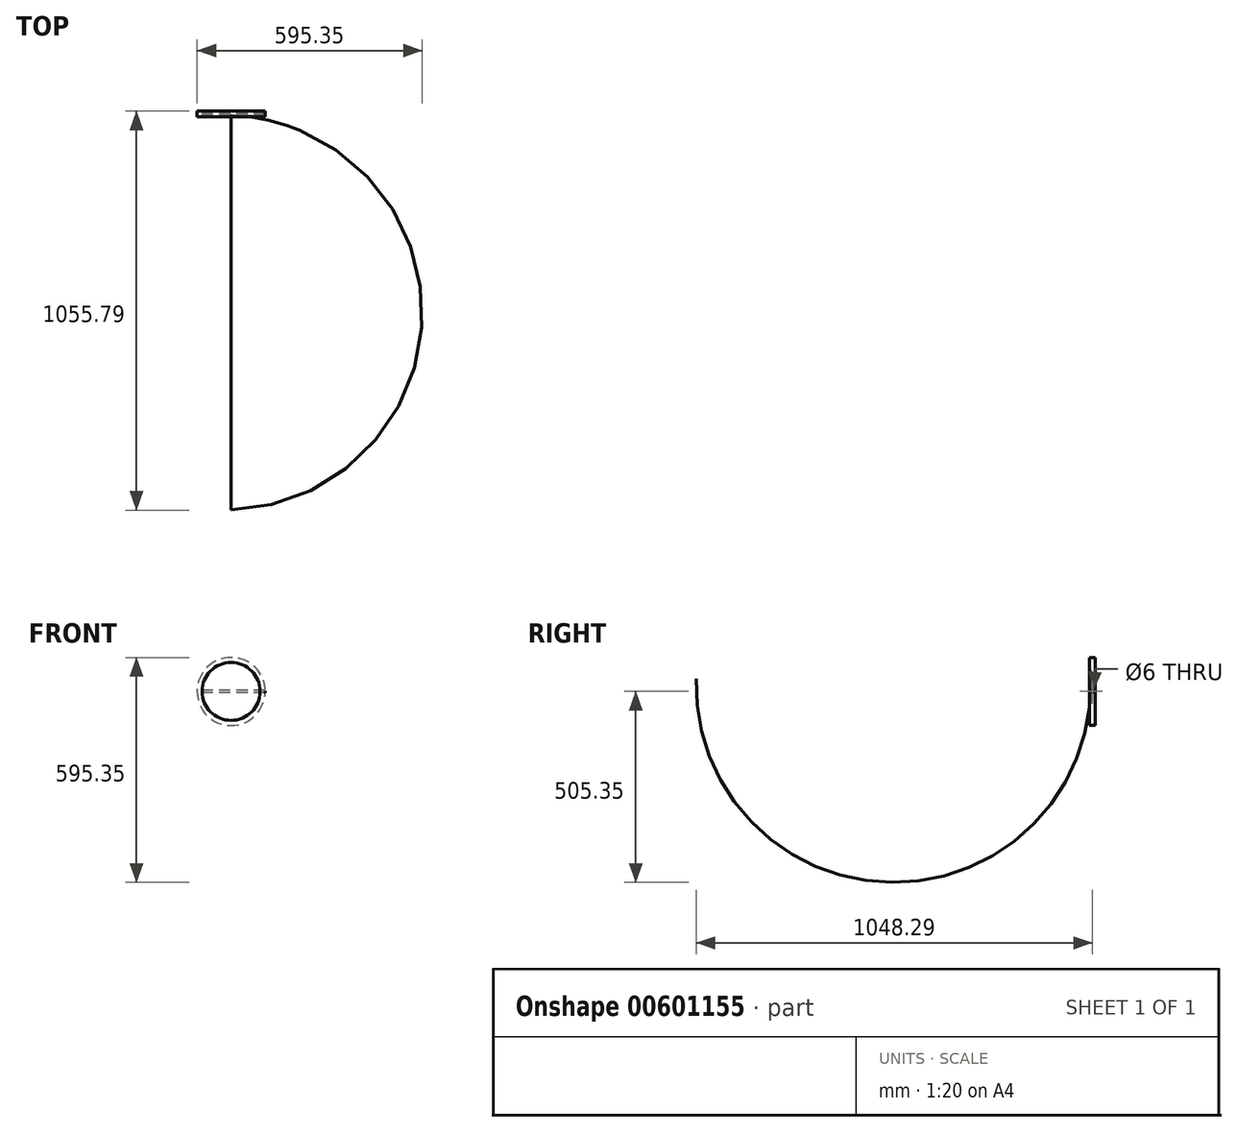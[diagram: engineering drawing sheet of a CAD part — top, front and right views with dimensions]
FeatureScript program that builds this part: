
annotation { "Feature Type Name" : "Feature", "Feature Type Description" : "" }
export const myFeature = defineFeature(function(context is Context, id is Id, definition is map)
    precondition{}
    {
        {
            var Q0;
            Q0=qCreatedBy(makeId("Front.planeOp"),FACE);
            var sketch = newSketch(context, id + "F0", { "sketchPlane" : qUnion([Q0])});
            skCircle(sketch, "E0", {"center": v(0, 0) * mm, "radius": 90 * mm});
            skSolve(sketch);
        }
        {
            var Q0;
            Q0=qSketchRegion(id+"F0",true);
            extrude(context, id + "F1", {"entities" : qUnion([Q0]), "depth" : 15 * mm, "offsetDistance" : 25 * mm, "symmetric" : true});
        }
        {
            var Q0;
            Q0=qCreatedBy(makeId("Right.planeOp"),FACE);
            var sketch = newSketch(context, id + "F2", { "sketchPlane" : qUnion([Q0])});
            skCircle(sketch, "E1", {"center": v(0, 0) * mm, "radius": 3 * mm});
            skSolve(sketch);
        }
        {
            var Q0;
            Q0=qSketchRegion(id+"F2",true);
            extrude(context, id + "F3", {"entities" : qUnion([Q0]), "operationType" : NewBodyOperationType.REMOVE, "depth" : 180 * mm, "offsetDistance" : 25 * mm, "symmetric" : true});
        }
        {
            var Q0;
            Q0=qCreatedBy(makeId("Right.planeOp"),FACE);
            var sketch = newSketch(context, id + "F4", { "sketchPlane" : qUnion([Q0])});
            skLineSegment(sketch, "E2", {"start": v(-30.38, 0) * mm, "end": v(32.5, 0) * mm});
            skSolve(sketch);
        }
        {
            var Q0;
            Q0=qCreatedBy(makeId("Right.planeOp"),FACE);
            var sketch = newSketch(context, id + "F5", { "sketchPlane" : qUnion([Q0])});
            skLineSegment(sketch, "E3", {"start": v(-7.9, 0) * mm, "end": v(-4.33, 0) * mm});
            skLineSegment(sketch, "E4", {"start": v(-7.9, 0) * mm, "end": v(-7.9, 80) * mm});
            skArc(sketch, "E5", {"start": v(-4.33, 0) * mm, "mid": v(-4.58, 40.07) * mm, "end": v(-7.9, 80) * mm});
            skSolve(sketch);
        }
        {
            var Q0;
            Q0=qSketchRegion(id+"F5",true);
            var Q1;
            Q1=sQuery(id+"F4.wireOp",EDGE,"E2");
            revolve(context, id + "F6", {"operationType" : NewBodyOperationType.REMOVE, "entities" : qUnion([Q0]), "axis" : qUnion([Q1]), "revolveType" : RevolveType.FULL, "oppositeDirection" : true});
        }
    });
